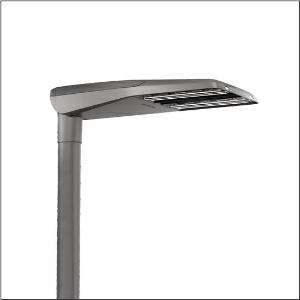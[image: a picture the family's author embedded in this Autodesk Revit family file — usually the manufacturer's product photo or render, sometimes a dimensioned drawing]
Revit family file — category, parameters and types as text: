
# Revit family: streetlight_sl_11_iq_midi___st1_2a_5xc3a41f08le_475e
name_source: partatom
category: Lighting Fixtures
units: mm (PartAtom-declared; Revit-internal decimal feet)

## family parameters
Cut with Voids When Loaded = No
Host = Face
Light Source = No
Part Type = Normal
Room Calculation Point = No
Round Connector Dimension = Use Diameter
Shared = No

## types (1)
- --- (1 x LED, 9590 lm, 60.4 W, 4000K)
    Apparent Load = 60 VA
    CIE Flux Codes = 32 70 96 100 100
    Color Rendering = 70
    Color Temperature = 4000K
    Default Elevation = 1800 mm
    Description = Streetlight SL 11 iQ midi, mast luminaire, primary light control with 3 zone facetted reflector, of plastic, silver coated, highly specular, primary optical cover: cover, of PMMA, transparent, light distribution: ST1.2a, light emission: direct distribution, primary light characteristic: asymmetric, installation type: post-top, side-entry, LED, High Power LED, rated luminous flux: 9.590lm, luminous efficacy: 159lm/W, light colour: 740, colour temperature: 4000K, control: Street-Remote, optimised constant luminous flux control (CLO 2.0), Desk-Remote (wireless, voltage-free reading and setting of iQ features in the workshop via application-optimized NFC function/RFID function), Light-Fading, Smart-Wire, Night-Set, Lumen-Switch, Temp-Guard, Auto-Match, with cable H07RN-F 5x 1.5mm², mains connection: 230..240V, AC, 50/60Hz, connection cable pre-assembled, cable length: 8,5m, start of lifetime: 60W, end of service life: 63W, reduction: 30W, luminaire housing, of diecast aluminium, powder-coated, Siteco® metallic grey (DB 702S), please order mast flange separately, inclination adjustable without tools: 0°, 5°, 10°, 15° (post-top) | 0°, -5°, -10°, -15° (side-entry), sealing non-destructively replaceable, multi-level sealing system, length: 780mm, width: 376mm, height: 118mm, mast flange for spigot size: 42mm (side-entry): 5XC10008XM4, 60/48mm (side-entry/post-top): 5XC10108XM2, 76/60mm (side-entry/post-top): 5XC10108XM1, equipment: standard, protection rating (complete): IP66, insulation class (complete): insulation class II (safety insulation), certification: CE, ENEC, VDE, impact resistance: IK09, permissible operating ambient temperature for outdoor applications: -25..+50°C, standard-compliant lighting for roads and squares, Environmental Product Declaration (EPD) tested and certified by an independent institute, packaging unit: 1 piece

Light Distribution: ST1.2a
    Height = 118 mm
    Lamp = 1 x LED
    Lamp Light Flux = 9590 lm
    Lamp Power = 60.4 W
    Lamp count = 1
    Length = 780 mm
    Luminous efficacy = 159 lm/W
    Manufacturer = Siteco
    ModVariant = No
    Model = 5XC3A41F08LE
    Number of Poles = 1
    OnlyDefault = Yes
    Power Factor = 1
    Product Name = Streetlight SL 11 iQ midi | ST1.2a
    Product group = mast luminaire | pylon top
    ProductGroupID = 6100
    Protection Class = Protection class II
    Protection Degree = IP 66
    RLX_Detail_Level = 1
    RLX_Emergency_Light_Flux = 0 lm
    RLX_Emergency_Type = 0
    RLX_Emergency_Type_DB = No
    RlxData = <blob elided: 70597 chars, md5=994e2455>
    Socket = socket
    Standby Power = 0 W
    System Light Flux = 9590 lm
    System Power = 60 W
    Type Comments = factory setting: luminous flux: 100 % | dim-lin: 254 | 520 mA
    Type Image = l_1005960.jpg
    URL = http://relux.com
    VarID = @adj_150791
    Voltage = 0 V
    Weight = 0.00 kg
    Width = 376 mm

## geometry (parser evidence)
native form markers: Blend x4, Sweep x9
no freeform markers — native parametric forms only
